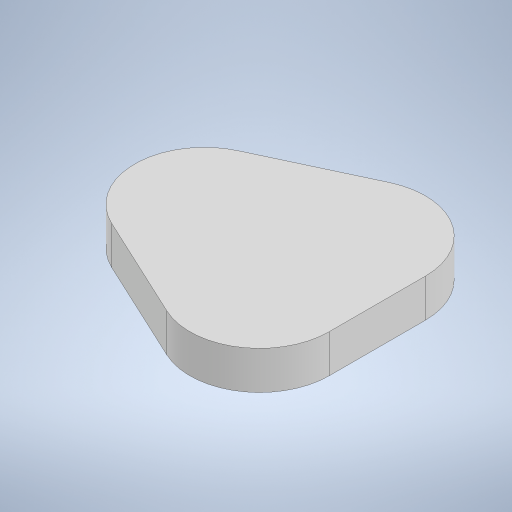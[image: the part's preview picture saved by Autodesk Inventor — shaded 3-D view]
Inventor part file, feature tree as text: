
AUTODESK INVENTOR PART (.ipt)
format: ipt  version: 2024.3 (Build 283343000, 343)  size: 251,904 bytes
history: native  units: in
note: dims shown in document units (in); Inventor stores cm internally (conversion verified against a paired STEP export)
features: extrude x2, sketch x2, projected_geometry x1
ambient origin geometry x8: Origin, YZ Plane, XZ Plane, XY Plane, X Axis, Y Axis, Z Axis, Center Point
bodies: Solid1 (feature_tree)
feature tree (5):
  extrude  "Extrusion1"  Depth=0.0787in TaperAngle=0.0deg
  extrude  "Extrusion2"  Depth=0.1181in
  sketch  "Sketch1"  dims[d4=0.3543in d5=0.0in d6=0.0787in d7=0.0in]
  sketch  "Sketch2"  dims[d9=0.3436in d10=1.0551in d11=1.4843in d12=1.0551in d13=1.0551in d14=0.1181in d15=0.1181in d8=0.0197in]
  projected_geometry  "Projected Loop2"
